# Revit family: Увлажнитель с погружным электродом AIRNED-M UE
name_source: partatom
category: Оборудование
revit_build: Autodesk Revit 2017 (Build: 20160225_1515(x64)
units: mm (PartAtom-declared; Revit-internal decimal feet)

## family parameters
Всегда вертикально = Да
На основе рабочей плоскости = Нет
Общий = Нет
При загрузке вырезать с полостями = Нет
Размер круглого соединителя = Использовать диаметр
Тип детали = Нормальный
Точка расчета площади = Нет

## types (14) — shared parameters
Единица измерения = шт.
Завод изготовитель = NED
Ключевая пометка = Вентиляция
Материал = Сталь серая
Наименование и тех.хар-ка = Увлажнитель с погружным электродом
Раздел = ОВ

## per-type parameters (varying)
| type | А | А1 | Б | В1 | Номинальная паропроизводительность, кг/ч | Потребляемая мощность, кВт | Размер В | Тип, марка, обозначение |
| AIRNED-M UE 001 | 545 мм | 491 мм | 815 мм | 334 мм | 35 мм | 26 Вт | 371 мм | AIRNED-M UE 035 |
| AIRNED-M UE 003 | 365 мм | 329 мм | 712 мм | 248 мм | 3 мм | 2 Вт | 275 мм | AIRNED-M UE 003 |
| AIRNED-M UE 005 | 365 мм | 329 мм | 712 мм | 248 мм | 5 мм | 4 Вт | 275 мм | AIRNED-M UE 005 |
| AIRNED-M UE 008 | 365 мм | 329 мм | 712 мм | 248 мм | 8 мм | 6 Вт | 275 мм | AIRNED-M UE 008 |
| AIRNED-M UE 009 | 365 мм | 329 мм | 712 мм | 248 мм | 9 мм | 7 Вт | 275 мм | AIRNED-M UE 009 |
| AIRNED-M UE 010 | 365 мм | 329 мм | 712 мм | 248 мм | 10 мм | 8 Вт | 275 мм | AIRNED-M UE 010 |
| AIRNED-M UE 015 | 365 мм | 329 мм | 712 мм | 248 мм | 15 мм | 11 Вт | 275 мм | AIRNED-M UE 015 |
| AIRNED-M UE 018 | 365 мм | 329 мм | 712 мм | 248 мм | 18 мм | 14 Вт | 275 мм | AIRNED-M UE 018 |
| AIRNED-M UE 025 | 545 мм | 491 мм | 815 мм | 338 мм | 25 мм | 19 Вт | 375 мм | AIRNED-M UE 025 |
| AIRNED-M UE 035 | 545 мм | 491 мм | 815 мм | 334 мм | 35 мм | 26 Вт | 371 мм | AIRNED-M UE 035 |
| AIRNED-M UE 045 | 545 мм | 491 мм | 815 мм | 338 мм | 45 мм | 34 Вт | 375 мм | AIRNED-M UE 045 |
| AIRNED-M UE 065 | 635 мм | 572 мм | 890 мм | 419 мм | 65 мм | 49 Вт | 465 мм | AIRNED-M UE 065 |
| AIRNED-M UE 090 | 1150 мм | 1035 мм | 890 мм | 419 мм | 90 мм | 68 Вт | 465 мм | AIRNED-M UE 090 |
| AIRNED-M UE 130 | 1150 мм | 1035 мм | 890 мм | 419 мм | 130 мм | 98 Вт | 465 мм | AIRNED-M UE 130 |
